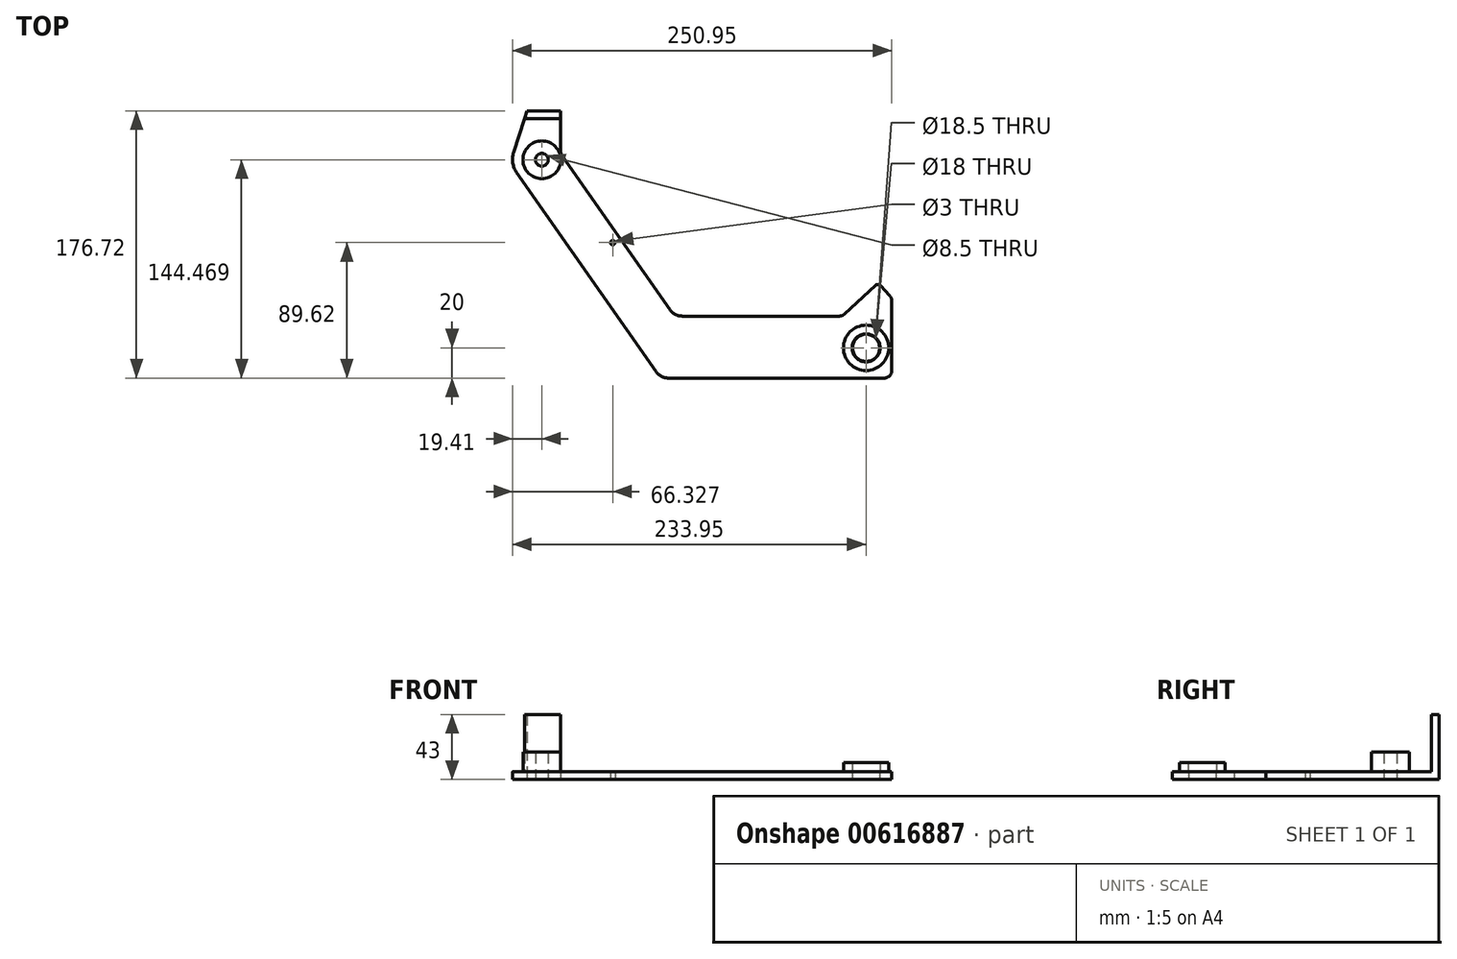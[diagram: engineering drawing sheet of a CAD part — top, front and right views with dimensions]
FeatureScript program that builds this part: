
annotation { "Feature Type Name" : "Feature", "Feature Type Description" : "" }
export const myFeature = defineFeature(function(context is Context, id is Id, definition is map)
    precondition{}
    {
        {
            var Q0;
            Q0=qCreatedBy(makeId("Top.planeOp"),FACE);
            var sketch = newSketch(context, id + "F0", { "sketchPlane" : qUnion([Q0])});
            skLineSegment(sketch, "E0", {"start": v(-5, 0) * mm, "end": v(-147.8, 0) * mm});
            skLineSegment(sketch, "E1", {"start": v(-155.99, 4.26) * mm, "end": v(-248.24, 136.01) * mm});
            skLineSegment(sketch, "E2", {"start": v(-250.21, 149.25) * mm, "end": v(-241.29, 176.72) * mm});
            skLineSegment(sketch, "E3", {"start": v(-241.29, 176.72) * mm, "end": v(-219.29, 176.72) * mm});
            skLineSegment(sketch, "E4", {"start": v(-219.29, 176.72) * mm, "end": v(-219.29, 151.87) * mm});
            skLineSegment(sketch, "E5", {"start": v(-217.48, 146.14) * mm, "end": v(-146.85, 45.26) * mm});
            skLineSegment(sketch, "E6", {"start": v(-138.66, 41) * mm, "end": v(-34.73, 41) * mm});
            skLineSegment(sketch, "E7", {"start": v(-31.32, 42.34) * mm, "end": v(-11.04, 61.26) * mm});
            skLineSegment(sketch, "E8", {"start": v(-7.5, 61.13) * mm, "end": v(-1.34, 54.53) * mm});
            skLineSegment(sketch, "E9", {"start": v(0, 51.12) * mm, "end": v(0, 5) * mm});
            skPoint(sketch, "E10.visualSharp", {"position": v(-252.53, 142.14) * mm});
            skArc(sketch, "E10.filletArc", {"start": v(-250.21, 149.25) * mm, "mid": v(-250.78, 142.4) * mm, "end": v(-248.24, 136.01) * mm});
            skPoint(sketch, "E11.visualSharp", {"position": v(-153, 0) * mm});
            skArc(sketch, "E11.filletArc", {"start": v(-155.99, 4.26) * mm, "mid": v(-152.41, 1.13) * mm, "end": v(-147.8, 0) * mm});
            skPoint(sketch, "E12.visualSharp", {"position": v(0, 0) * mm});
            skArc(sketch, "E12.filletArc", {"start": v(-5, 0) * mm, "mid": v(-1.46, 1.46) * mm, "end": v(0, 5) * mm});
            skPoint(sketch, "E13.visualSharp", {"position": v(-32.76, 41) * mm});
            skPoint(sketch, "E14.visualSharp", {"position": v(-9.2, 62.96) * mm});
            skPoint(sketch, "E15.visualSharp", {"position": v(0, 53.09) * mm});
            skArc(sketch, "E15.filletArc", {"start": v(0, 51.12) * mm, "mid": v(-0.35, 52.95) * mm, "end": v(-1.34, 54.53) * mm});
            skPoint(sketch, "E16.visualSharp", {"position": v(-143.86, 41) * mm});
            skArc(sketch, "E16.filletArc", {"start": v(-146.85, 45.26) * mm, "mid": v(-143.28, 42.13) * mm, "end": v(-138.66, 41) * mm});
            skPoint(sketch, "E17.visualSharp", {"position": v(-219.29, 148.72) * mm});
            skArc(sketch, "E17.filletArc", {"start": v(-219.29, 151.87) * mm, "mid": v(-218.83, 148.86) * mm, "end": v(-217.48, 146.14) * mm});
            skCircle(sketch, "E18", {"center": v(-17, 20) * mm, "radius": 9 * mm});
            skCircle(sketch, "E19", {"center": v(-231.54, 144.47) * mm, "radius": 4.25 * mm, "construction": true});
            skCircle(sketch, "E20", {"center": v(-231.54, 144.47) * mm, "radius": 12.5 * mm, "construction": true});
            skCircle(sketch, "E21", {"center": v(-184.62, 89.62) * mm, "radius": 1.5 * mm});
            skLineSegment(sketch, "E22", {"start": v(-184.62, 89.62) * mm, "end": v(-180.12, 92.78) * mm, "construction": true});
            skArc(sketch, "E23.filletArc", {"start": v(-7.5, 61.13) * mm, "mid": v(-9.24, 61.93) * mm, "end": v(-11.04, 61.26) * mm});
            skArc(sketch, "E24.filletArc", {"start": v(-34.73, 41) * mm, "mid": v(-32.9, 41.35) * mm, "end": v(-31.32, 42.34) * mm});
            skSolve(sketch);
        }
        {
            var Q0;
            Q0=qSketchRegion(id+"F0",true);
            extrude(context, id + "F1", {"entities" : qUnion([Q0]), "depth" : 5 * mm, "offsetDistance" : 25 * mm});
        }
        {
            var Q0;
            Q0=makeQuery(id+"F1.opExtrude","CAP_FACE",FACE,{"disambiguationData":[OSD([sQuery(id+"F0.wireOp",EDGE,"E0"),sQuery(id+"F0.wireOp",EDGE,"E1"),sQuery(id+"F0.wireOp",EDGE,"E2"),sQuery(id+"F0.wireOp",EDGE,"E3"),sQuery(id+"F0.wireOp",EDGE,"E4"),sQuery(id+"F0.wireOp",EDGE,"E5"),sQuery(id+"F0.wireOp",EDGE,"E6"),sQuery(id+"F0.wireOp",EDGE,"E7"),sQuery(id+"F0.wireOp",EDGE,"E8"),sQuery(id+"F0.wireOp",EDGE,"E9"),sQuery(id+"F0.wireOp",EDGE,"E10.filletArc"),sQuery(id+"F0.wireOp",EDGE,"E11.filletArc"),sQuery(id+"F0.wireOp",EDGE,"E12.filletArc"),sQuery(id+"F0.wireOp",EDGE,"E13.filletArc"),sQuery(id+"F0.wireOp",EDGE,"E14.filletArc"),sQuery(id+"F0.wireOp",EDGE,"E15.filletArc"),sQuery(id+"F0.wireOp",EDGE,"E16.filletArc"),sQuery(id+"F0.wireOp",EDGE,"E17.filletArc"),sQuery(id+"F0.wireOp",EDGE,"E18"),sQuery(id+"F0.wireOp",EDGE,"E21")])],"isStart":true});
            var sketch = newSketch(context, id + "F2", { "sketchPlane" : qUnion([Q0])});
            skLineSegment(sketch, "E25.0", {"start": v(-241.29, -176.72) * mm, "end": v(-219.29, -176.72) * mm});
            skLineSegment(sketch, "E26.0", {"start": v(-219.29, -176.72) * mm, "end": v(-219.29, -171.72) * mm});
            skLineSegment(sketch, "E27.0", {"start": v(-242.91, -171.72) * mm, "end": v(-241.29, -176.72) * mm});
            skLineSegment(sketch, "E28", {"start": v(-219.29, -171.72) * mm, "end": v(-242.91, -171.72) * mm});
            skSolve(sketch);
        }
        {
            var Q0;
            Q0=qSketchRegion(id+"F2",true);
            extrude(context, id + "F3", {"entities" : qUnion([Q0]), "operationType" : NewBodyOperationType.ADD, "oppositeDirection" : true, "depth" : 43 * mm, "offsetDistance" : 25 * mm});
        }
        {
            var Q0;
            Q0=makeQuery(id+"F0.imprint","IMPRINT",FACE,{"disambiguationData":[TD([[makeQuery(id+"F0.imprint","IMPRINT",EDGE,{"derivedFrom":sQuery(id+"F0.wireOp",EDGE,"E0")}),-1.0]])]});
            var sketch = newSketch(context, id + "F4", { "sketchPlane" : qUnion([Q0])});
            skCircle(sketch, "E29.0", {"center": v(-231.54, 144.47) * mm, "radius": 12.5 * mm});
            skSolve(sketch);
        }
        {
            var Q0;
            Q0=qSketchRegion(id+"F4",true);
            extrude(context, id + "F5", {"entities" : qUnion([Q0]), "operationType" : NewBodyOperationType.ADD, "depth" : 18 * mm, "offsetDistance" : 25 * mm, "hasSecondDirection" : true, "secondDirectionOppositeDirection" : false, "secondDirectionDepth" : 5 * mm});
        }
        {
            var Q0;
            Q0=makeQuery(id+"F1.opExtrude","CAP_FACE",FACE,{"disambiguationData":[OSD([sQuery(id+"F0.wireOp",EDGE,"E0"),sQuery(id+"F0.wireOp",EDGE,"E1"),sQuery(id+"F0.wireOp",EDGE,"E2"),sQuery(id+"F0.wireOp",EDGE,"E3"),sQuery(id+"F0.wireOp",EDGE,"E4"),sQuery(id+"F0.wireOp",EDGE,"E5"),sQuery(id+"F0.wireOp",EDGE,"E6"),sQuery(id+"F0.wireOp",EDGE,"E7"),sQuery(id+"F0.wireOp",EDGE,"E8"),sQuery(id+"F0.wireOp",EDGE,"E9"),sQuery(id+"F0.wireOp",EDGE,"E10.filletArc"),sQuery(id+"F0.wireOp",EDGE,"E11.filletArc"),sQuery(id+"F0.wireOp",EDGE,"E12.filletArc"),sQuery(id+"F0.wireOp",EDGE,"E13.filletArc"),sQuery(id+"F0.wireOp",EDGE,"E14.filletArc"),sQuery(id+"F0.wireOp",EDGE,"E15.filletArc"),sQuery(id+"F0.wireOp",EDGE,"E16.filletArc"),sQuery(id+"F0.wireOp",EDGE,"E17.filletArc"),sQuery(id+"F0.wireOp",EDGE,"E18"),sQuery(id+"F0.wireOp",EDGE,"E21")])],"isStart":false});
            var sketch = newSketch(context, id + "F6", { "sketchPlane" : qUnion([Q0])});
            skCircle(sketch, "E30.0", {"center": v(-231.54, 144.47) * mm, "radius": 4.25 * mm});
            skSolve(sketch);
        }
        {
            var Q0;
            Q0=makeQuery(id+"F6.imprint","IMPRINT",FACE,{"disambiguationData":[TD([[makeQuery(id+"F6.imprint","IMPRINT",EDGE,{"derivedFrom":sQuery(id+"F6.wireOp",EDGE,"E30.0")}),1.0]])]});
            extrude(context, id + "F7", {"entities" : qUnion([Q0]), "operationType" : NewBodyOperationType.REMOVE, "endBound" : BoundingType.THROUGH_ALL, "depth" : 21.5 * mm, "offsetDistance" : 25 * mm, "hasSecondDirection" : true, "secondDirectionBound" : BoundingType.THROUGH_ALL, "secondDirectionOppositeDirection" : true, "secondDirectionDepth" : 25 * mm});
        }
        {
            var Q0;
            Q0=makeQuery(id+"F1.opExtrude","CAP_FACE",FACE,{"disambiguationData":[OSD([sQuery(id+"F0.wireOp",EDGE,"E0"),sQuery(id+"F0.wireOp",EDGE,"E1"),sQuery(id+"F0.wireOp",EDGE,"E2"),sQuery(id+"F0.wireOp",EDGE,"E3"),sQuery(id+"F0.wireOp",EDGE,"E4"),sQuery(id+"F0.wireOp",EDGE,"E5"),sQuery(id+"F0.wireOp",EDGE,"E6"),sQuery(id+"F0.wireOp",EDGE,"E7"),sQuery(id+"F0.wireOp",EDGE,"E8"),sQuery(id+"F0.wireOp",EDGE,"E9"),sQuery(id+"F0.wireOp",EDGE,"E10.filletArc"),sQuery(id+"F0.wireOp",EDGE,"E11.filletArc"),sQuery(id+"F0.wireOp",EDGE,"E12.filletArc"),sQuery(id+"F0.wireOp",EDGE,"E15.filletArc"),sQuery(id+"F0.wireOp",EDGE,"E16.filletArc"),sQuery(id+"F0.wireOp",EDGE,"E17.filletArc"),sQuery(id+"F0.wireOp",EDGE,"E18"),sQuery(id+"F0.wireOp",EDGE,"E21"),sQuery(id+"F0.wireOp",EDGE,"E23.filletArc"),sQuery(id+"F0.wireOp",EDGE,"E24.filletArc")])],"isStart":false});
            var sketch = newSketch(context, id + "F8", { "sketchPlane" : qUnion([Q0])});
            skCircle(sketch, "E31", {"center": v(-17, 20) * mm, "radius": 15 * mm});
            skCircle(sketch, "E32.0", {"center": v(-17, 20) * mm, "radius": 9 * mm, "construction": true});
            skCircle(sketch, "E33", {"center": v(-17, 20) * mm, "radius": 9.25 * mm});
            skSolve(sketch);
        }
        {
            var Q0;
            Q0=makeQuery(id+"F8.imprint","IMPRINT",FACE,{"disambiguationData":[TD([[makeQuery(id+"F8.imprint","IMPRINT",EDGE,{"derivedFrom":sQuery(id+"F8.wireOp",EDGE,"E31")}),1.0]])]});
            extrude(context, id + "F9", {"entities" : qUnion([Q0]), "depth" : 6 * mm, "offsetDistance" : 25 * mm});
        }
    });
